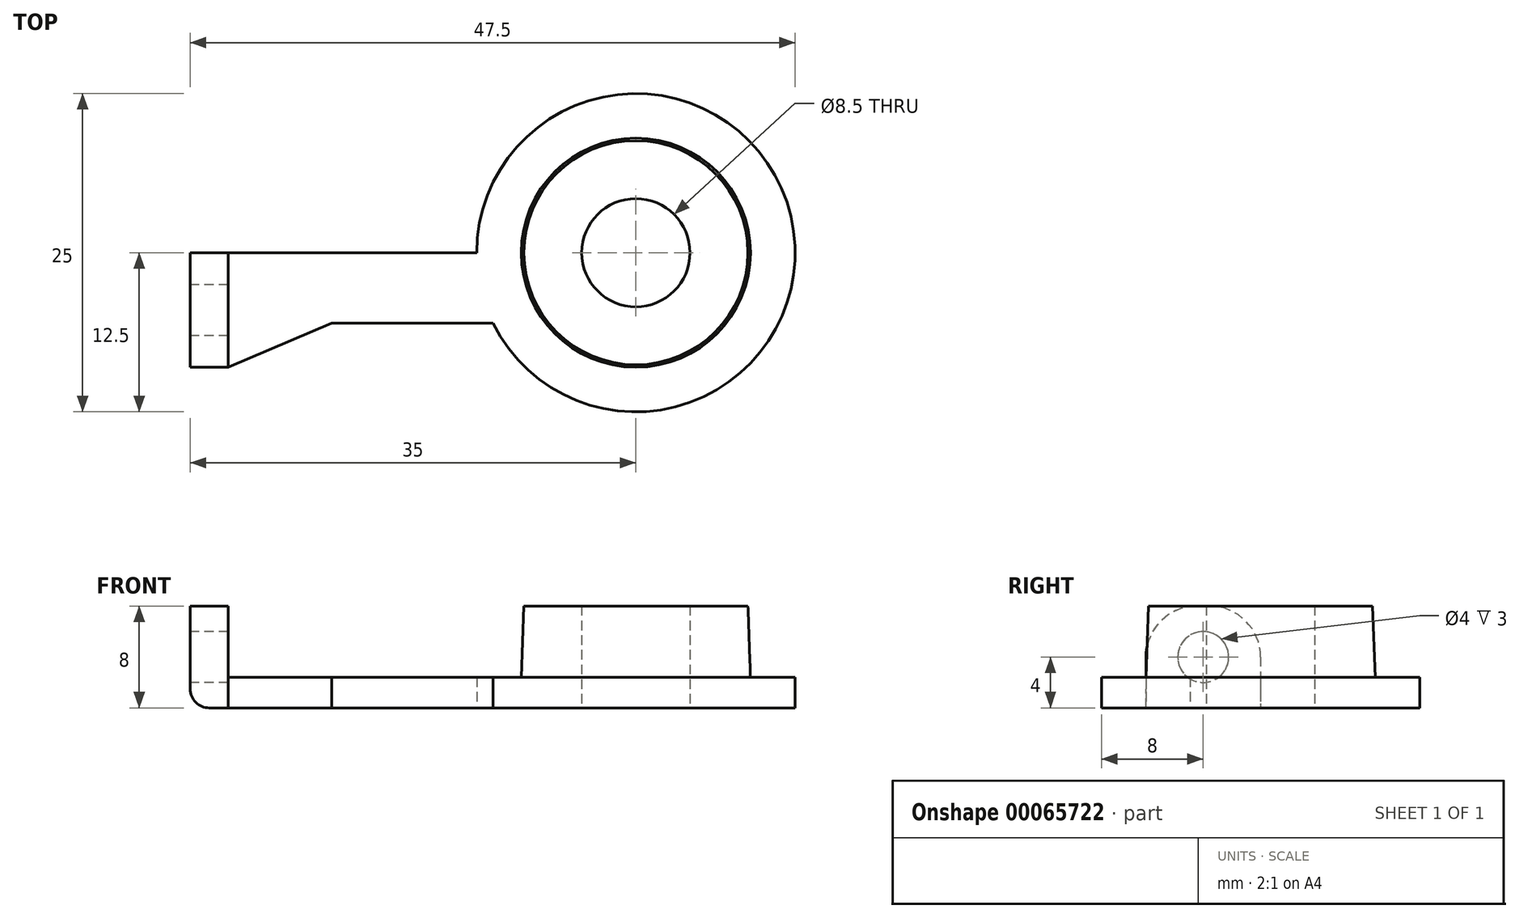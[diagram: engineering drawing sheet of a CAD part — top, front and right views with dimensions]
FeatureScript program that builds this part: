
annotation { "Feature Type Name" : "Feature", "Feature Type Description" : "" }
export const myFeature = defineFeature(function(context is Context, id is Id, definition is map)
    precondition{}
    {
        {
            var Q0;
            Q0=qCreatedBy(makeId("Top.planeOp"),FACE);
            var sketch = newSketch(context, id + "F0", { "sketchPlane" : qUnion([Q0])});
            skCircle(sketch, "E0", {"center": v(0, 0) * mm, "radius": 9 * mm});
            skCircle(sketch, "E1.0", {"center": v(0, 0) * mm, "radius": 6.9 * mm});
            skCircle(sketch, "E2", {"center": v(0, 0) * mm, "radius": 4.25 * mm});
            skLineSegment(sketch, "E3", {"start": v(0, 0) * mm, "end": v(-35, 0) * mm});
            skLineSegment(sketch, "E4", {"start": v(-35, 0) * mm, "end": v(-35, -9) * mm});
            skLineSegment(sketch, "E5", {"start": v(-35, -9) * mm, "end": v(0, -9) * mm});
            skLineSegment(sketch, "E6", {"start": v(-35, -4.5) * mm, "end": v(-32, -4.5) * mm, "construction": true});
            skLineSegment(sketch, "E7", {"start": v(-32, -9) * mm, "end": v(-32, 0) * mm});
            skLineSegment(sketch, "E8", {"start": v(-32, -9) * mm, "end": v(-23.87, -5.54) * mm});
            skLineSegment(sketch, "E9", {"start": v(-23.87, -5.54) * mm, "end": v(0, -5.54) * mm});
            skCircle(sketch, "E10", {"center": v(0, 0) * mm, "radius": 12.5 * mm});
            skSolve(sketch);
        }
        {
            var Q0;
            Q0=makeQuery(id+"F0.imprint","IMPRINT",FACE,{"disambiguationData":[TD([[makeQuery(id+"F0.imprint","IMPRINT",EDGE,{"derivedFrom":sQuery(id+"F0.wireOp",EDGE,"E1.0")}),-1.0]])]});
            var Q1;
            {var subQ5=sQuery(id+"F0.wireOp",EDGE,"E7");Q1=makeQuery(id+"F0.imprint","IMPRINT",FACE,{"disambiguationData":[TD([[makeQuery(id+"F0.imprint","IMPRINT",EDGE,{"derivedFrom":subQ5}),-1.0]])]});}
            var Q2;
            {var subQ5=sQuery(id+"F0.wireOp",EDGE,"E0");var subQ7=makeQuery(id+"F0.imprint","INTERSECT",VERTEX,{"derivedFrom":[subQ5,sQuery(id+"F0.wireOp",EDGE,"E5")]});Q2=makeQuery(id+"F0.imprint","IMPRINT",FACE,{"disambiguationData":[TD([[makeQuery(id+"F0.imprint","IMPRINT",EDGE,{"disambiguationData":[TD([[subQ7,1.0]])],"derivedFrom":subQ5}),1.0]])]});}
            var Q3;
            {var subQ0=sQuery(id+"F0.wireOp",EDGE,"E5");var subQ1=sQuery(id+"F0.wireOp",EDGE,"E0");var subQ2=makeQuery(id+"F0.imprint","INTERSECT",VERTEX,{"derivedFrom":[subQ1,subQ0]});Q3=makeQuery(id+"F0.imprint","IMPRINT",FACE,{"disambiguationData":[TD([[makeQuery(id+"F0.imprint","IMPRINT",EDGE,{"disambiguationData":[TD([[subQ2,-1.0]])],"derivedFrom":subQ1}),-1.0]])]});}
            var Q4;
            {var subQ0=sQuery(id+"F0.wireOp",EDGE,"E9");var subQ1=sQuery(id+"F0.wireOp",EDGE,"E0");var subQ2=makeQuery(id+"F0.imprint","INTERSECT",VERTEX,{"derivedFrom":[subQ1,subQ0]});Q4=makeQuery(id+"F0.imprint","IMPRINT",FACE,{"disambiguationData":[TD([[makeQuery(id+"F0.imprint","IMPRINT",EDGE,{"disambiguationData":[TD([[subQ2,1.0]])],"derivedFrom":subQ1}),-1.0]])]});}
            var Q5;
            {var subQ0=sQuery(id+"F0.wireOp",EDGE,"E5");var subQ1=sQuery(id+"F0.wireOp",EDGE,"E0");var subQ2=makeQuery(id+"F0.imprint","INTERSECT",VERTEX,{"derivedFrom":[subQ1,subQ0]});Q5=makeQuery(id+"F0.imprint","IMPRINT",FACE,{"disambiguationData":[TD([[makeQuery(id+"F0.imprint","IMPRINT",EDGE,{"disambiguationData":[TD([[subQ2,1.0]])],"derivedFrom":subQ1}),-1.0]])]});}
            extrude(context, id + "F1", {"entities" : qUnion([Q0, Q1, Q2, Q3, Q4, Q5]), "depth" : 2.4 * mm});
        }
        {
            var Q0;
            Q0=makeQuery(id+"F0.imprint","IMPRINT",FACE,{"disambiguationData":[TD([[makeQuery(id+"F0.imprint","IMPRINT",EDGE,{"derivedFrom":sQuery(id+"F0.wireOp",EDGE,"E1.0")}),1.0]])]});
            var Q1;
            {var subQ0=sQuery(id+"F0.wireOp",EDGE,"E4");Q1=makeQuery(id+"F0.imprint","IMPRINT",FACE,{"disambiguationData":[TD([[makeQuery(id+"F0.imprint","IMPRINT",EDGE,{"derivedFrom":subQ0}),1.0]])]});}
            var Q2;
            {var subQ5=sQuery(id+"F0.wireOp",EDGE,"E0");var subQ6=makeQuery(id+"F0.imprint","INTERSECT",VERTEX,{"derivedFrom":[subQ5,sQuery(id+"F0.wireOp",EDGE,"E5")]});Q2=makeQuery(id+"F0.imprint","IMPRINT",FACE,{"disambiguationData":[TD([[makeQuery(id+"F0.imprint","IMPRINT",EDGE,{"disambiguationData":[TD([[subQ6,1.0]])],"derivedFrom":subQ5}),1.0]])]});}
            var Q3;
            {var subQ0=sQuery(id+"F0.wireOp",EDGE,"E9");var subQ1=sQuery(id+"F0.wireOp",EDGE,"E0");var subQ2=makeQuery(id+"F0.imprint","INTERSECT",VERTEX,{"derivedFrom":[subQ1,subQ0]});Q3=makeQuery(id+"F0.imprint","IMPRINT",FACE,{"disambiguationData":[TD([[makeQuery(id+"F0.imprint","IMPRINT",EDGE,{"disambiguationData":[TD([[subQ2,1.0]])],"derivedFrom":subQ1}),1.0]])]});}
            extrude(context, id + "F2", {"entities" : qUnion([Q0, Q1, Q2, Q3]), "operationType" : NewBodyOperationType.ADD, "depth" : 8 * mm});
        }
        {
            var Q0;
            Q0=makeQuery(id+"F2.opExtrude","SWEPT_FACE",FACE,{"disambiguationData":[OSD([sQuery(id+"F0.wireOp",EDGE,"E4")])]});
            cPlane(context, id + "F3", {"entities" : qUnion([Q0]), "cplaneType" : CPlaneType.OFFSET, "offset" : 0 * mm, "width" : 150 * mm, "height" : 150 * mm});
        }
        {
            var Q0;
            Q0=qCreatedBy(id+"F3.planeOp",FACE);
            var sketch = newSketch(context, id + "F4", { "sketchPlane" : qUnion([Q0])});
            skLineSegment(sketch, "E11", {"start": v(0, 0) * mm, "end": v(-4.5, 0) * mm, "construction": true});
            skLineSegment(sketch, "E12", {"start": v(-4.5, 0) * mm, "end": v(-4.5, 4) * mm, "construction": true});
            skCircle(sketch, "E13.MirrorC", {"center": v(4.5, 4) * mm, "radius": 2 * mm});
            skSolve(sketch);
        }
        {
            var Q0;
            Q0 = qSketchRegion(id + "F4", true);
            var Q1;
            Q1=makeQuery(id+"F2.opExtrude","SWEPT_FACE",FACE,{"disambiguationData":[OSD([sQuery(id+"F0.wireOp",EDGE,"E7")])]});
            extrude(context, id + "F5", {"entities" : qUnion([Q0]), "operationType" : NewBodyOperationType.REMOVE, "endBound" : BoundingType.UP_TO_SURFACE, "oppositeDirection" : true, "endBoundEntityFace" : qUnion([Q1]), "depth" : 25 * mm});
        }
        {
            var Q0;
            Q0=makeQuery(id+"F2.opExtrude","CAP_EDGE",EDGE,{"disambiguationData":[OSD([sQuery(id+"F0.wireOp",EDGE,"E5")])],"isStart":false});
            var Q1;
            Q1=makeQuery(id+"F2.opExtrude","CAP_EDGE",EDGE,{"disambiguationData":[OSD([sQuery(id+"F0.wireOp",EDGE,"E3")])],"isStart":false});
            fillet(context, id + "F6", {"entities" : qUnion([Q0, Q1]), "radius" : 4 * mm, "tangentPropagation" : true, "allowEdgeOverflow" : false});
        }
        {
            var Q0;
            Q0=makeQuery(id+"F2.opExtrude","CAP_EDGE",EDGE,{"disambiguationData":[OSD([sQuery(id+"F0.wireOp",EDGE,"E4")])],"isStart":true});
            var Q1;
            {var subQ0=sQuery(id+"F0.wireOp",EDGE,"E5");Q1=makeQuery(id+"F2.boolean.opBoolean","MERGE",EDGE,{"derivedFrom":[makeQuery(id+"F1.opExtrude","CAP_EDGE",EDGE,{"disambiguationData":[OSD([subQ0])],"isStart":true}),makeQuery(id+"F2.opExtrude","CAP_EDGE",EDGE,{"disambiguationData":[OSD([subQ0])],"isStart":true})]});}
            fillet(context, id + "F7", {"entities" : qUnion([Q0, Q1]), "radius" : 1.5 * mm, "tangentPropagation" : true, "allowEdgeOverflow" : false});
        }
        {
            var Q0;
            Q0=makeQuery(id+"F2.opExtrude","CAP_EDGE",EDGE,{"disambiguationData":[OSD([sQuery(id+"F0.wireOp",EDGE,"E0")])],"isStart":false});
            chamfer(context, id + "F8", {"entities" : qUnion([Q0]), "chamferType" : ChamferType.OFFSET_ANGLE, "width" : 0.2 * mm, "oppositeDirection" : false, "angle" : 88 * degree, "tangentPropagation" : true});
        }
    });
